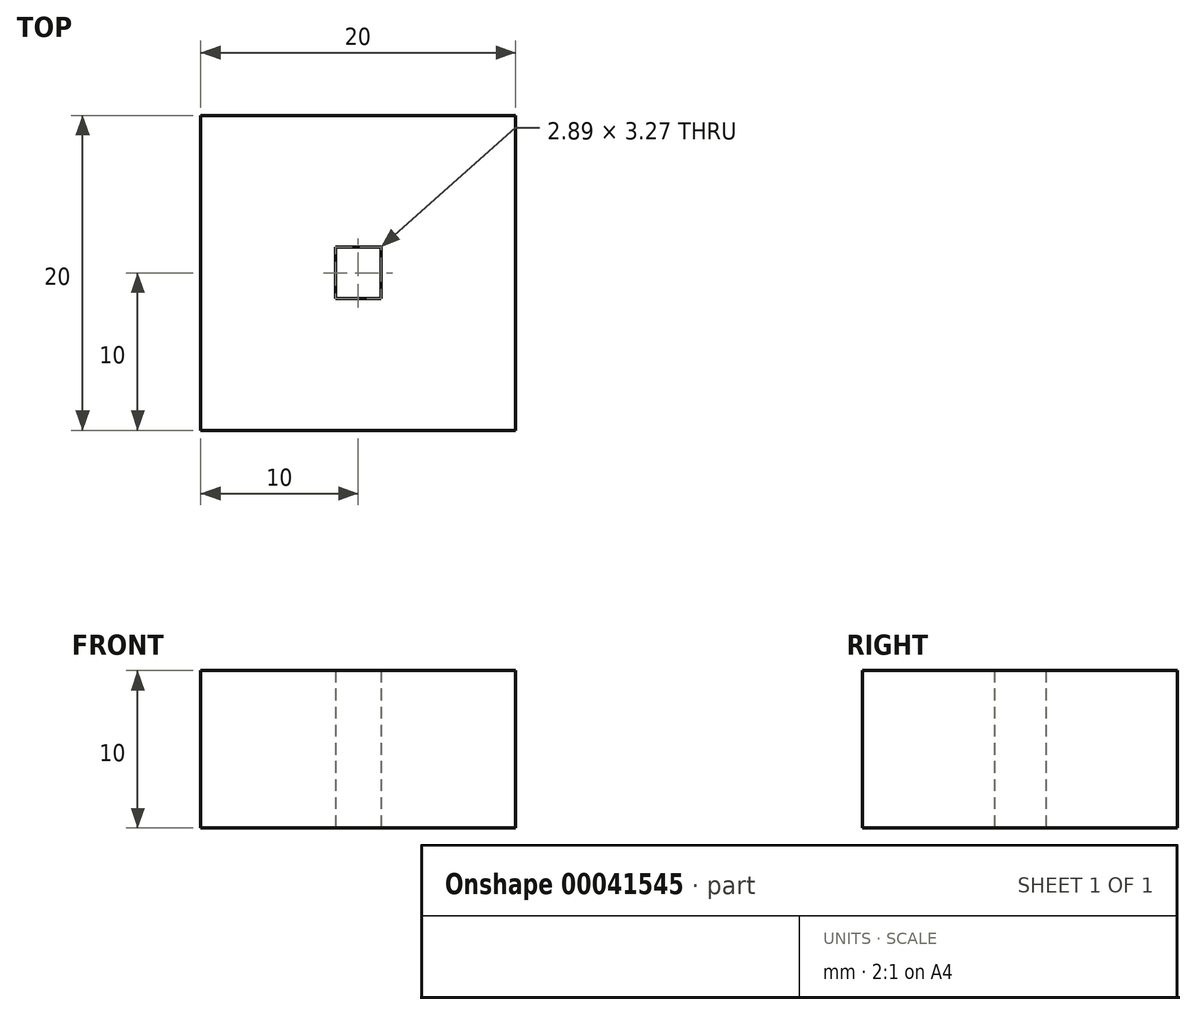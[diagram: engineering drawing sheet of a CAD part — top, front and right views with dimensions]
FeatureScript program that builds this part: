
annotation { "Feature Type Name" : "Feature", "Feature Type Description" : "" }
export const myFeature = defineFeature(function(context is Context, id is Id, definition is map)
    precondition{}
    {
        {
            var Q0;
            Q0=qCreatedBy(makeId("Top.planeOp"),FACE);
            var sketch = newSketch(context, id + "F0", { "sketchPlane" : qUnion([Q0])});
            skLineSegment(sketch, "E0.rect.bottom", {"start": v(10, -10) * mm, "end": v(-10, -10) * mm});
            skLineSegment(sketch, "E0.rect.top", {"start": v(10, 10) * mm, "end": v(-10, 10) * mm});
            skLineSegment(sketch, "E0.rect.left", {"start": v(10, -10) * mm, "end": v(10, 10) * mm});
            skLineSegment(sketch, "E0.rect.right", {"start": v(-10, -10) * mm, "end": v(-10, 10) * mm});
            skPoint(sketch, "E0.rect.middle", {"position": v(0, 0) * mm});
            skLineSegment(sketch, "E1.rect.bottom", {"start": v(1.44, -1.64) * mm, "end": v(-1.44, -1.64) * mm});
            skLineSegment(sketch, "E1.rect.top", {"start": v(1.44, 1.64) * mm, "end": v(-1.44, 1.63) * mm});
            skLineSegment(sketch, "E1.rect.left", {"start": v(1.44, -1.63) * mm, "end": v(1.44, 1.64) * mm});
            skLineSegment(sketch, "E1.rect.right", {"start": v(-1.44, -1.64) * mm, "end": v(-1.44, 1.64) * mm});
            skSolve(sketch);
        }
        {
            var Q0;
            Q0 = qSketchRegion(id + "F0", true);
            extrude(context, id + "F1", {"entities" : qUnion([Q0]), "depth" : 10 * mm});
        }
    });
